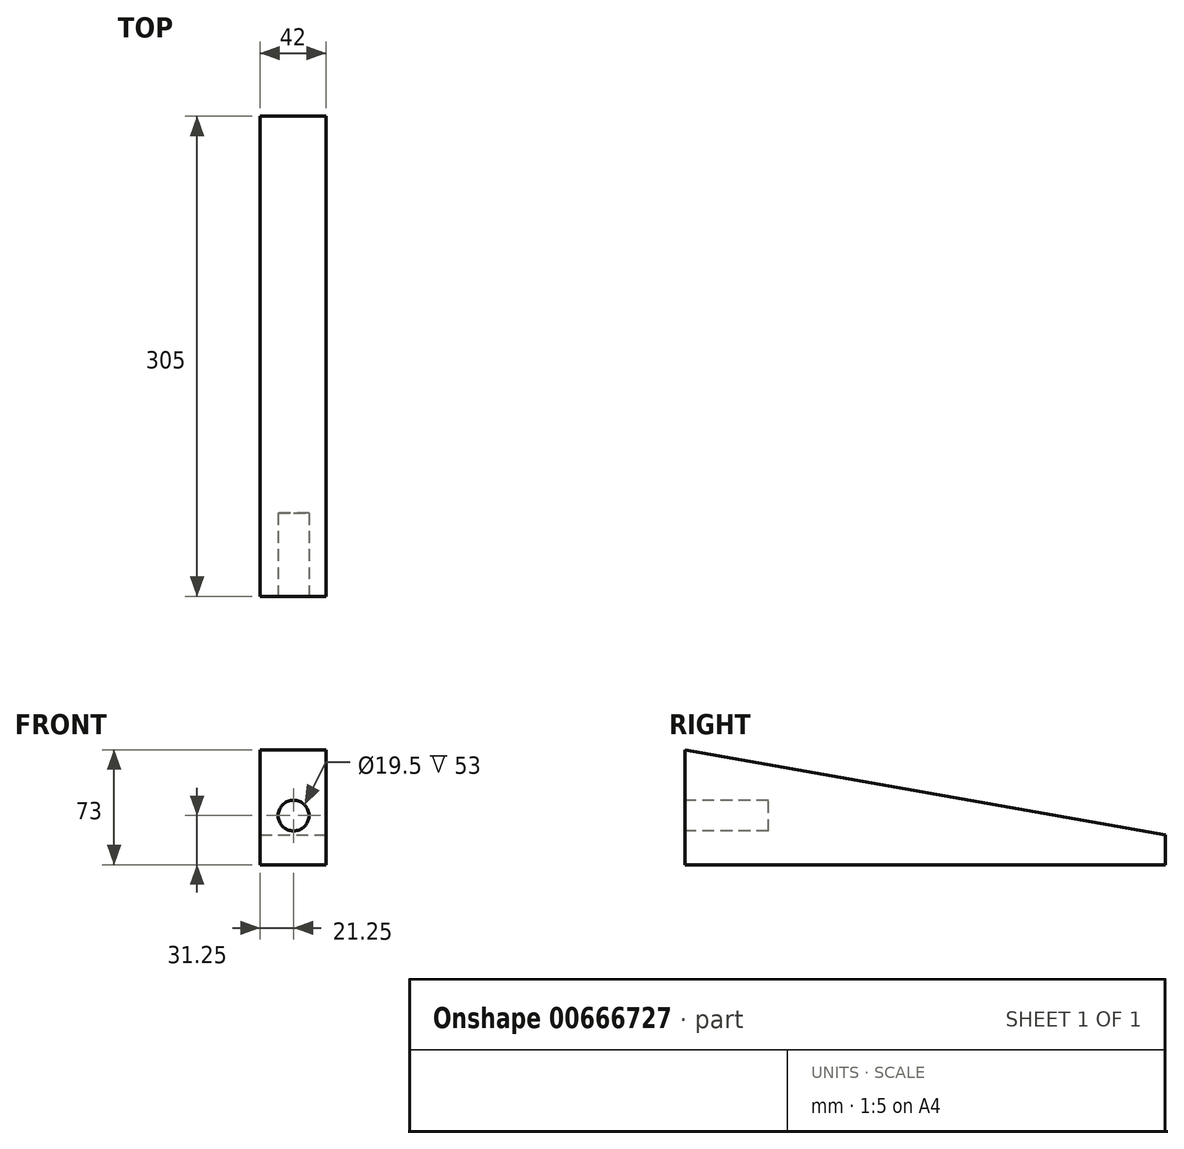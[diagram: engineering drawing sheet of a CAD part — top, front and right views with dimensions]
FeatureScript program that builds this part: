
annotation { "Feature Type Name" : "Feature", "Feature Type Description" : "" }
export const myFeature = defineFeature(function(context is Context, id is Id, definition is map)
    precondition{}
    {
        {
            var Q0;
            Q0=qCreatedBy(makeId("Front.planeOp"),FACE);
            var sketch = newSketch(context, id + "F0", { "sketchPlane" : qUnion([Q0])});
            skLineSegment(sketch, "E0.bottom", {"start": v(0, 0) * mm, "end": v(42, 0) * mm});
            skLineSegment(sketch, "E0.top", {"start": v(0, 73) * mm, "end": v(42, 73) * mm});
            skLineSegment(sketch, "E0.left", {"start": v(0, 0) * mm, "end": v(0, 73) * mm});
            skLineSegment(sketch, "E0.right", {"start": v(42, 0) * mm, "end": v(42, 73) * mm});
            skSolve(sketch);
        }
        {
            var Q0;
            Q0=makeQuery(id+"F0.imprint","IMPRINT",FACE,{"disambiguationData":[TD([[makeQuery(id+"F0.imprint","IMPRINT",EDGE,{"derivedFrom":sQuery(id+"F0.wireOp",EDGE,"E0.bottom")}),1.0]])]});
            extrude(context, id + "F1", {"entities" : qUnion([Q0]), "oppositeDirection" : true, "depth" : 305 * mm, "offsetDistance" : 25 * mm});
        }
        {
            var Q0;
            Q0=makeQuery(id+"F1.opExtrude","SWEPT_FACE",FACE,{"disambiguationData":[OSD([sQuery(id+"F0.wireOp",EDGE,"E0.right")])]});
            var sketch = newSketch(context, id + "F2", { "sketchPlane" : qUnion([Q0])});
            skLineSegment(sketch, "E1", {"start": v(305, 0) * mm, "end": v(305, 19) * mm});
            skLineSegment(sketch, "E2", {"start": v(305, 19) * mm, "end": v(0, 73) * mm});
            skLineSegment(sketch, "E3", {"start": v(0, 73) * mm, "end": v(305, 73) * mm});
            skLineSegment(sketch, "E4", {"start": v(305, 73) * mm, "end": v(305, 19) * mm});
            skSolve(sketch);
        }
        {
            var Q0;
            Q0=makeQuery(id+"F2.imprint","IMPRINT",FACE,{"disambiguationData":[TD([[makeQuery(id+"F2.imprint","IMPRINT",EDGE,{"derivedFrom":sQuery(id+"F2.wireOp",EDGE,"E2")}),-1.0]])]});
            extrude(context, id + "F3", {"entities" : qUnion([Q0]), "operationType" : NewBodyOperationType.REMOVE, "oppositeDirection" : true, "depth" : 42 * mm, "offsetDistance" : 25 * mm});
        }
        {
            var Q0;
            Q0=makeQuery(id+"F1.opExtrude","CAP_FACE",FACE,{"disambiguationData":[OSD([sQuery(id+"F0.wireOp",EDGE,"E0.bottom"),sQuery(id+"F0.wireOp",EDGE,"E0.top"),sQuery(id+"F0.wireOp",EDGE,"E0.left"),sQuery(id+"F0.wireOp",EDGE,"E0.right")])],"isStart":true});
            var sketch = newSketch(context, id + "F4", { "sketchPlane" : qUnion([Q0])});
            skCircle(sketch, "E5", {"center": v(21.25, 31.25) * mm, "radius": 9.75 * mm});
            skLineSegment(sketch, "E6", {"start": v(31, 31.25) * mm, "end": v(42, 31.25) * mm});
            skLineSegment(sketch, "E7", {"start": v(21.25, 21.5) * mm, "end": v(21.25, 0) * mm});
            skLineSegment(sketch, "E8", {"start": v(11.5, 31.25) * mm, "end": v(0, 31.25) * mm});
            skPoint(sketch, "E8.endSnap0", {"position": v(0, 36.5) * mm});
            skLineSegment(sketch, "E9", {"start": v(21.25, 41) * mm, "end": v(21.25, 73) * mm});
            skSolve(sketch);
        }
        {
            var Q0;
            {var subQ0=sQuery(id+"F4.wireOp",EDGE,"E5");var subQ1=makeQuery(id+"F4.imprint","INTERSECT",VERTEX,{"derivedFrom":[subQ0,sQuery(id+"F4.wireOp",EDGE,"E6")]});Q0=makeQuery(id+"F4.imprint","IMPRINT",FACE,{"disambiguationData":[TD([[makeQuery(id+"F4.imprint","IMPRINT",EDGE,{"disambiguationData":[TD([[subQ1,-1.0]])],"derivedFrom":subQ0}),1.0]])]});}
            extrude(context, id + "F5", {"entities" : qUnion([Q0]), "operationType" : NewBodyOperationType.REMOVE, "oppositeDirection" : true, "depth" : 53 * mm, "offsetDistance" : 25 * mm});
        }
    });
